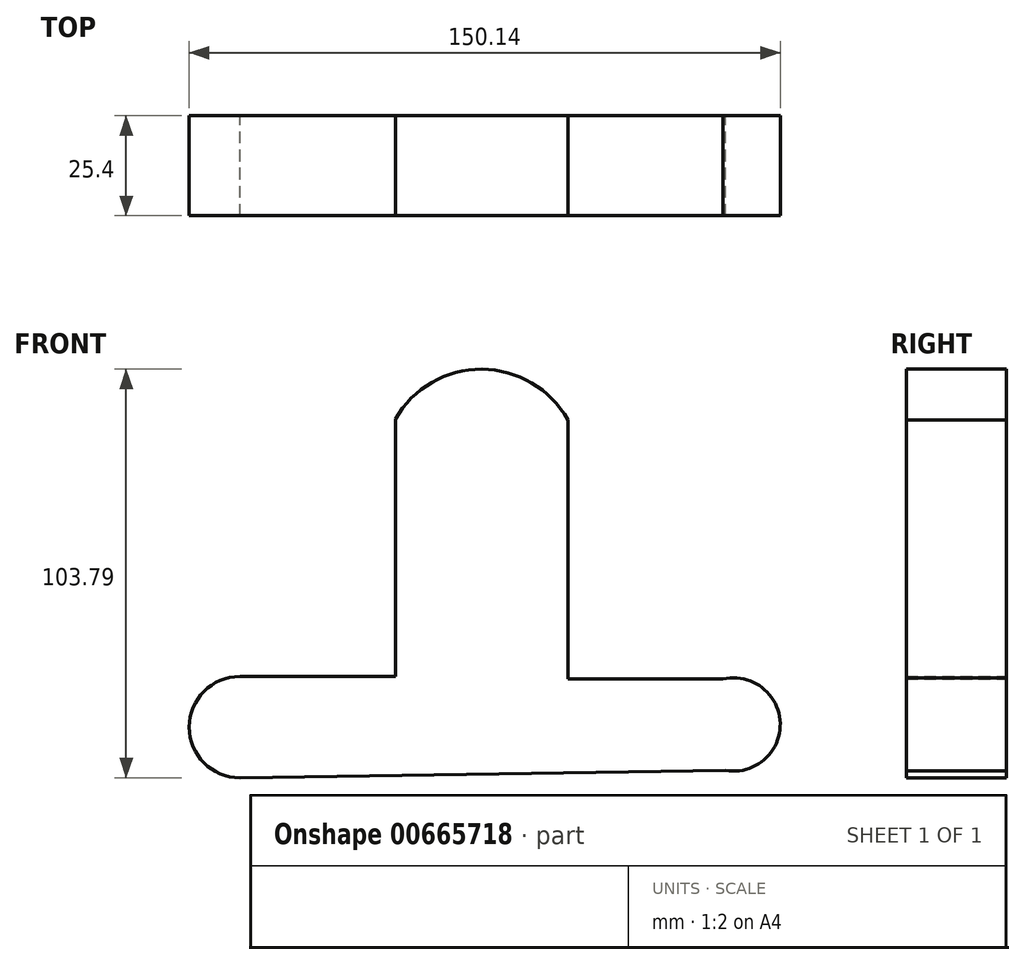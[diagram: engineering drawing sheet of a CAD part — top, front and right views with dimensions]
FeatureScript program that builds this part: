
annotation { "Feature Type Name" : "Feature", "Feature Type Description" : "" }
export const myFeature = defineFeature(function(context is Context, id is Id, definition is map)
    precondition{}
    {
        {
            var Q0;
            Q0=qCreatedBy(makeId("Front.planeOp"),FACE);
            var sketch = newSketch(context, id + "F0", { "sketchPlane" : qUnion([Q0])});
            skLineSegment(sketch, "E0", {"start": v(-26.64, -9.36) * mm, "end": v(-26.64, 56.05) * mm});
            skLineSegment(sketch, "E1", {"start": v(17.17, -9.98) * mm, "end": v(17.17, 55.84) * mm});
            skLineSegment(sketch, "E2", {"start": v(-26.64, -9.36) * mm, "end": v(-59.75, -9.36) * mm});
            skLineSegment(sketch, "E3", {"start": v(17.17, -9.98) * mm, "end": v(56.67, -9.98) * mm});
            skLineSegment(sketch, "E4", {"start": v(-59.75, -9.36) * mm, "end": v(-66.13, -9.36) * mm});
            skArc(sketch, "E5", {"start": v(-66.13, -9.36) * mm, "mid": v(-78.98, -22.21) * mm, "end": v(-66.13, -35.07) * mm});
            skLineSegment(sketch, "E6", {"start": v(-66.13, -35.07) * mm, "end": v(57.28, -33.22) * mm});
            skArc(sketch, "E7", {"start": v(57.28, -33.22) * mm, "mid": v(71.16, -21.22) * mm, "end": v(56.67, -9.98) * mm});
            skArc(sketch, "E8", {"start": v(17.17, 55.84) * mm, "mid": v(-4.67, 68.72) * mm, "end": v(-26.64, 56.05) * mm});
            skSolve(sketch);
        }
        {
            var Q0;
            Q0 = qSketchRegion(id + "F0", true);
            extrude(context, id + "F1", {"entities" : qUnion([Q0]), "depth" : 25.4 * mm, "offsetDistance" : 25.4 * mm});
        }
    });
